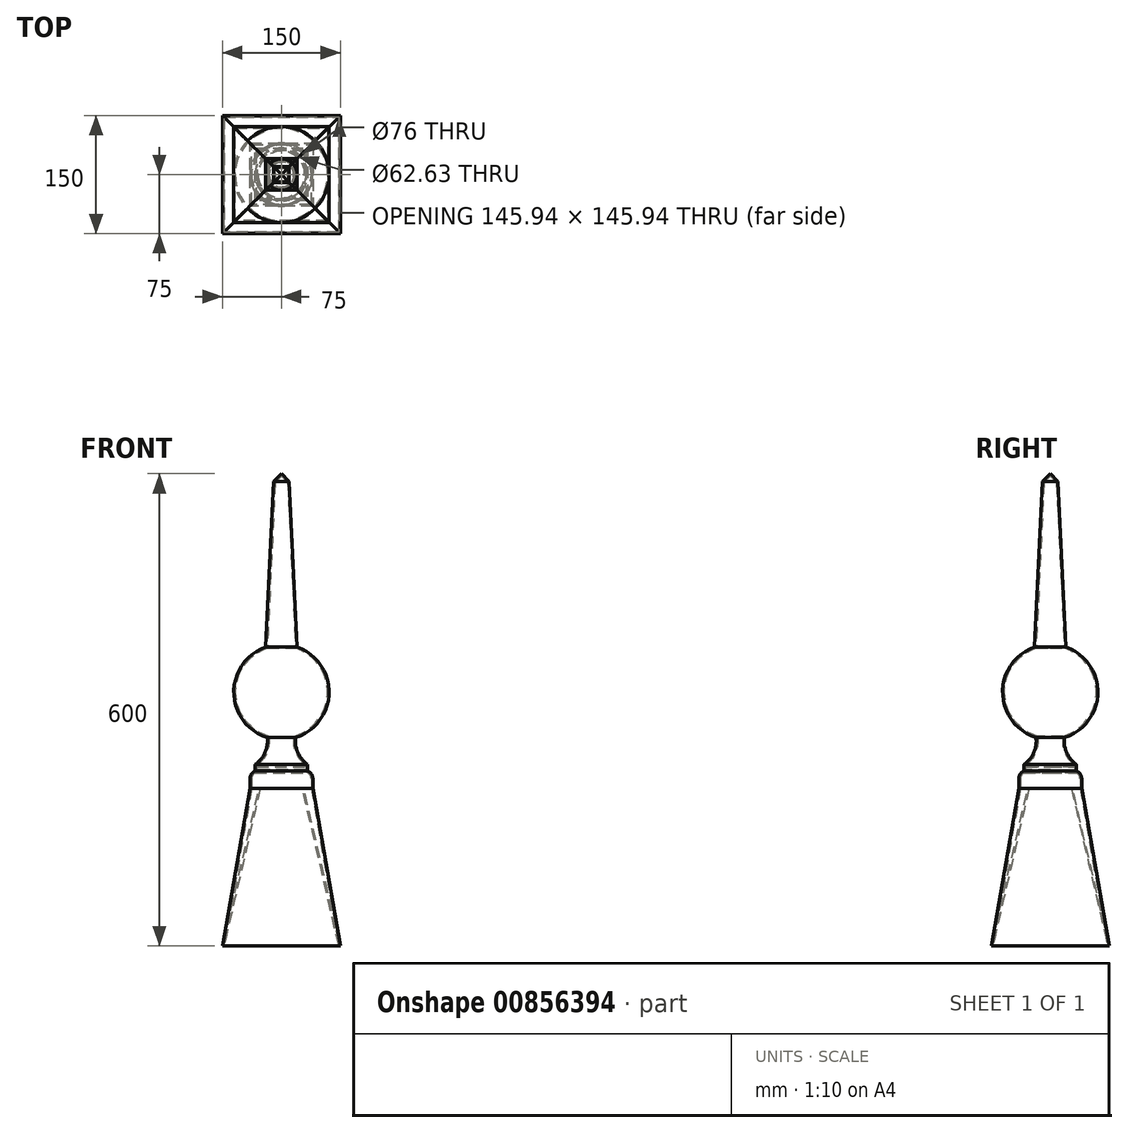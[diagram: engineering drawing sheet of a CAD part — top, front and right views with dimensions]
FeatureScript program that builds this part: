
annotation { "Feature Type Name" : "Feature", "Feature Type Description" : "" }
export const myFeature = defineFeature(function(context is Context, id is Id, definition is map)
    precondition{}
    {
        {
            var Q0;
            Q0=qCreatedBy(makeId("Front.planeOp"),FACE);
            var sketch = newSketch(context, id + "F0", { "sketchPlane" : qUnion([Q0])});
            skLineSegment(sketch, "E0", {"start": v(0, 0) * mm, "end": v(0, 689.54) * mm});
            skSolve(sketch);
        }
        {
            var Q0;
            Q0=qCreatedBy(makeId("Front.planeOp"),FACE);
            var sketch = newSketch(context, id + "F1", { "sketchPlane" : qUnion([Q0])});
            skLineSegment(sketch, "E1", {"start": v(0, 0) * mm, "end": v(0, 600) * mm});
            skLineSegment(sketch, "E2", {"start": v(0, 0) * mm, "end": v(75, 0) * mm});
            skLineSegment(sketch, "E3", {"start": v(75, 0) * mm, "end": v(40, 200.41) * mm});
            skLineSegment(sketch, "E4", {"start": v(40, 200.41) * mm, "end": v(0, 200.41) * mm});
            skLineSegment(sketch, "E5", {"start": v(40, 200.41) * mm, "end": v(40, 212.41) * mm});
            skArc(sketch, "E6", {"start": v(40, 212.41) * mm, "mid": v(38.18, 218.43) * mm, "end": v(33.32, 222.41) * mm});
            skLineSegment(sketch, "E7", {"start": v(33.32, 222.41) * mm, "end": v(0, 222.41) * mm});
            skLineSegment(sketch, "E8", {"start": v(33.32, 222.41) * mm, "end": v(33.32, 230.41) * mm});
            skArc(sketch, "E9", {"start": v(18, 264.66) * mm, "mid": v(20.97, 245.44) * mm, "end": v(33.32, 230.41) * mm});
            skLineSegment(sketch, "E10", {"start": v(18, 264.66) * mm, "end": v(0, 264.66) * mm});
            skLineSegment(sketch, "E11", {"start": v(10, 590) * mm, "end": v(20, 380) * mm});
            skLineSegment(sketch, "E12", {"start": v(10, 590) * mm, "end": v(0, 600) * mm});
            skArc(sketch, "E13", {"start": v(0, 261.93) * mm, "mid": v(60.73, 322.66) * mm, "end": v(0, 383.39) * mm});
            skArc(sketch, "E14", {"start": v(0, 383.39) * mm, "mid": v(-60.73, 322.66) * mm, "end": v(0, 261.93) * mm});
            skSolve(sketch);
        }
        {
            var Q0;
            {var subQ0=sQuery(id+"F1.wireOp",EDGE,"E10");Q0=makeQuery(id+"F1.imprint","IMPRINT",FACE,{"disambiguationData":[TD([[makeQuery(id+"F1.imprint","IMPRINT",EDGE,{"derivedFrom":subQ0}),-1.0]])]});}
            var Q1;
            {var subQ0=sQuery(id+"F1.wireOp",EDGE,"E4");Q1=makeQuery(id+"F1.imprint","IMPRINT",FACE,{"disambiguationData":[TD([[makeQuery(id+"F1.imprint","IMPRINT",EDGE,{"derivedFrom":subQ0}),-1.0]])]});}
            var Q2;
            {var subQ1=sQuery(id+"F1.wireOp",EDGE,"E7");Q2=makeQuery(id+"F1.imprint","IMPRINT",FACE,{"disambiguationData":[TD([[makeQuery(id+"F1.imprint","IMPRINT",EDGE,{"derivedFrom":subQ1}),-1.0]])]});}
            var Q3;
            {var subQ0=sQuery(id+"F1.wireOp",EDGE,"E10");Q3=makeQuery(id+"F1.imprint","IMPRINT",FACE,{"disambiguationData":[TD([[makeQuery(id+"F1.imprint","IMPRINT",EDGE,{"derivedFrom":subQ0}),1.0]])]});}
            var Q4;
            {var subQ4=sQuery(id+"F1.wireOp",EDGE,"E11");Q4=makeQuery(id+"F1.imprint","IMPRINT",FACE,{"disambiguationData":[TD([[makeQuery(id+"F1.imprint","IMPRINT",EDGE,{"derivedFrom":subQ4}),-1.0]])]});}
            var Q5;
            Q5=sQuery(id+"F0.wireOp",EDGE,"E0");
            revolve(context, id + "F2", {"surfaceOperationType" : NewSurfaceOperationType.NEW, "entities" : qUnion([Q0, Q1, Q2, Q3, Q4]), "axis" : qUnion([Q5]), "revolveType" : RevolveType.FULL});
        }
        {
            var Q0;
            Q0=qCreatedBy(makeId("Top.planeOp"),FACE);
            var sketch = newSketch(context, id + "F3", { "sketchPlane" : qUnion([Q0])});
            skLineSegment(sketch, "E15.bottom", {"start": v(75, -75) * mm, "end": v(-75, -75) * mm});
            skLineSegment(sketch, "E15.top", {"start": v(75, 75) * mm, "end": v(-75, 75) * mm});
            skLineSegment(sketch, "E15.left", {"start": v(75, -75) * mm, "end": v(75, 75) * mm});
            skLineSegment(sketch, "E15.right", {"start": v(-75, -75) * mm, "end": v(-75, 75) * mm});
            skPoint(sketch, "E15.middle", {"position": v(0, 0) * mm});
            skSolve(sketch);
        }
        {
            var Q1;
            Q1=makeQuery(id+"F3.imprint","IMPRINT",FACE,{"disambiguationData":[TD([[makeQuery(id+"F3.imprint","IMPRINT",EDGE,{"derivedFrom":sQuery(id+"F3.wireOp",EDGE,"E15.bottom")}),-1.0]])]});
            var Q2;
            Q2=makeQuery(id+"F2.opRevolve","SWEPT_FACE",FACE,{"disambiguationData":[OSD([sQuery(id+"F1.wireOp",EDGE,"E4")])]});
            loft(context, id + "F4", {"operationType" : NewBodyOperationType.ADD, "sheetProfilesArray" : [{ "sheetProfileEntities" : qUnion([Q1]) }, { "sheetProfileEntities" : qUnion([Q2]) }]});
        }
        {
            var Q0;
            {var subQ4=sQuery(id+"F1.wireOp",EDGE,"E11");Q0=makeQuery(id+"F1.imprint","IMPRINT",FACE,{"disambiguationData":[TD([[makeQuery(id+"F1.imprint","IMPRINT",EDGE,{"derivedFrom":subQ4}),-1.0]])]});}
            var Q1;
            {var subQ0=sQuery(id+"F1.wireOp",EDGE,"E10");Q1=makeQuery(id+"F1.imprint","IMPRINT",FACE,{"disambiguationData":[TD([[makeQuery(id+"F1.imprint","IMPRINT",EDGE,{"derivedFrom":subQ0}),-1.0]])]});}
            var Q2;
            {var subQ1=sQuery(id+"F1.wireOp",EDGE,"E7");Q2=makeQuery(id+"F1.imprint","IMPRINT",FACE,{"disambiguationData":[TD([[makeQuery(id+"F1.imprint","IMPRINT",EDGE,{"derivedFrom":subQ1}),-1.0]])]});}
            var Q3;
            {var subQ0=sQuery(id+"F1.wireOp",EDGE,"E4");Q3=makeQuery(id+"F1.imprint","IMPRINT",FACE,{"disambiguationData":[TD([[makeQuery(id+"F1.imprint","IMPRINT",EDGE,{"derivedFrom":subQ0}),-1.0]])]});}
            var Q4;
            {var subQ0=sQuery(id+"F1.wireOp",EDGE,"E10");Q4=makeQuery(id+"F1.imprint","IMPRINT",FACE,{"disambiguationData":[TD([[makeQuery(id+"F1.imprint","IMPRINT",EDGE,{"derivedFrom":subQ0}),1.0]])]});}
            var Q5;
            {var subQ0=sQuery(id+"F1.wireOp",EDGE,"E2");Q5=makeQuery(id+"F1.imprint","IMPRINT",FACE,{"disambiguationData":[TD([[makeQuery(id+"F1.imprint","IMPRINT",EDGE,{"derivedFrom":subQ0}),1.0]])]});}
            var Q6;
            Q6 = qConstructionFilter(qBodyType(qCreatedBy(id + "F3" ,EDGE), BodyType.WIRE), ConstructionObject.NO);
            sweep(context, id + "F5", {"profiles" : qUnion([Q0, Q1, Q2, Q3, Q4, Q5]), "path" : qUnion([Q6])});
        }
        {
            var Q0;
            Q0=makeQuery(id+"F4.opLoft","CAP_FACE",FACE,{"disambiguationData":[OSD([makeQuery(id+"F3.imprint","IMPRINT",FACE,{"disambiguationData":[TD([[makeQuery(id+"F3.imprint","IMPRINT",EDGE,{"derivedFrom":sQuery(id+"F3.wireOp",EDGE,"E15.bottom")}),-1.0]])]})])],"isStart":true});
            shell(context, id + "F6", {"entities" : qUnion([Q0]), "thickness" : 2 * mm});
        }
        {
            var Q0;
            Q0=makeQuery(id+"F6.opShell","OFFSET_EDGE",EDGE,{"disambiguationData":[OSD([sQuery(id+"F1.wireOp",EDGE,"E6"),sQuery(id+"F1.wireOp",EDGE,"E7"),sQuery(id+"F1.wireOp",EDGE,"E8")])]});
            var Q1;
            Q1=makeQuery(id+"F6.opShell","OFFSET_EDGE",EDGE,{"disambiguationData":[OSD([sQuery(id+"F1.wireOp",EDGE,"E5"),sQuery(id+"F1.wireOp",EDGE,"E6")])]});
            var Q2;
            Q2=makeQuery(id+"F6.opShell","OFFSET_EDGE",EDGE,{"disambiguationData":[OSD([sQuery(id+"F1.wireOp",EDGE,"E8"),sQuery(id+"F1.wireOp",EDGE,"E9")])]});
            chamfer(context, id + "F7", {"entities" : qUnion([Q0, Q1, Q2]), "width" : 4.5 * mm, "tangentPropagation" : true});
        }
        {
            var Q0;
            Q0=makeQuery(id+"F5.opSweep","SWEPT_FACE",FACE,{"disambiguationData":[OSD([sQuery(id+"F1.wireOp",EDGE,"E2"),sQuery(id+"F3.wireOp",EDGE,"E15.bottom")])]});
            shell(context, id + "F8", {"entities" : qUnion([Q0]), "thickness" : 2 * mm});
        }
    });
